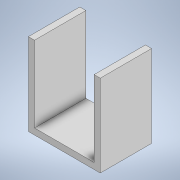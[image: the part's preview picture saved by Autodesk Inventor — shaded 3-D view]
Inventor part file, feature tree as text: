
AUTODESK INVENTOR PART (.ipt)
format: ipt  version: 2020 (Build 240168000, 168)  size: 96,256 bytes
history: native  units: mm
features: extrude x1, sketch x1
ambient origin geometry x8: Origin, YZ Plane, XZ Plane, XY Plane, X Axis, Y Axis, Z Axis, Center Point
bodies: Solid1 (feature_tree)
feature tree (2):
  extrude  "Extrusion1"  Depth=80.0mm
  sketch  "Sketch1"  dims[d0=70.0mm d1=80.0mm d2=80.0mm d3=6.0mm d4=50.0mm d5=0.0mm d6=0.5mm d7=0.872665mm]
